# Revit family: ARTLIGHT_Светильник светодиодный_ART-S(N)-FLUTE
name_source: partatom
category: Осветительные приборы
units: mm (PartAtom-declared; Revit-internal decimal feet)

## family parameters
Источник света = Да
Общий = Нет
Основа = Грань
При загрузке вырезать с полостями = Нет
Размер круглого соединителя = Использовать диаметр
Тип детали = Нормальный
Точка расчета площади = Нет

## types (9) — shared parameters
ADSK_Единица измерения = шт.
ADSK_Завод-изготовитель = ARTLIGHT
ADSK_Количество = 1
ADSK_Наименование = Светильник светодиодный
URL = https://artlight.ru
Отметка по умолчанию = 1219.2 мм
Подвес = Подвес
Полная установленная мощность = 0 В·А
Светильник = Стеклянная лампа
Светофильтр = 16777215
Смещение цветовой температуры при затухании лампы = <Нет>
Угол наклона = 90.00°
zero-valued in all types: ADSK_Масса

## per-type parameters (varying)
| type | Изображение типоразмера | Угол рассеивания | Файл фотометрической сетки |
| Белый 15° | ART-S-FLUTE w.jpeg | 15.00° | 15deg.ies |
| Белый 24° | ART-S-FLUTE w.jpeg | 24.00° | 24deg.ies |
| Белый 36° | ART-S-FLUTE w.jpeg | 36.00° | 36deg.ies |
| Черный 15° | ART-S-FLUTE b.jpeg | 15.00° | 15deg.ies |
| Черный 24° | ART-S-FLUTE b.jpeg | 24.00° | 24deg.ies |
| Черный 36° | ART-S-FLUTE b.jpeg | 36.00° | 36deg.ies |
| RAL 15° | ART-S-FLUTE w.jpeg | 15.00° | 15deg.ies |
| RAL 24° | ART-S-FLUTE w.jpeg | 24.00° | 24deg.ies |
| RAL 36° | ART-S-FLUTE w.jpeg | 36.00° | 36deg.ies |
